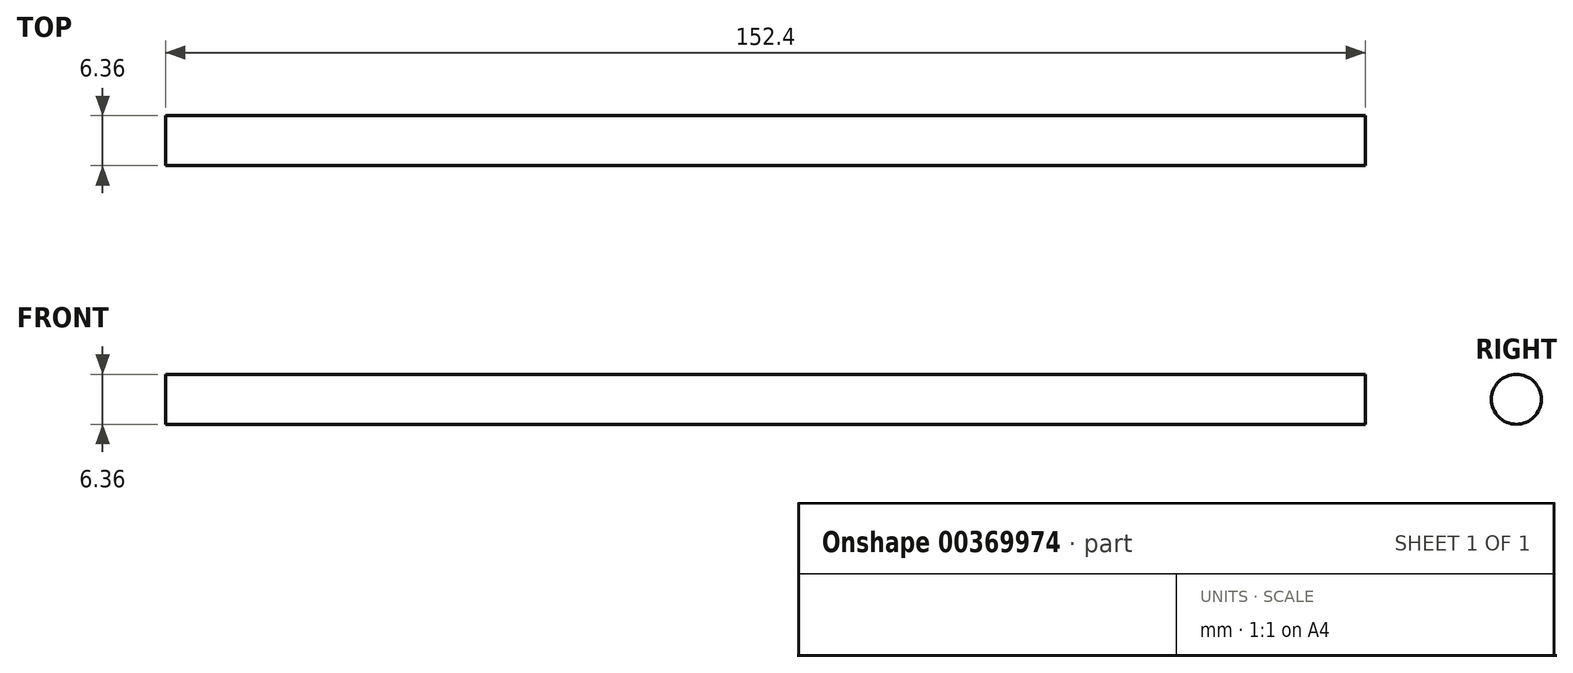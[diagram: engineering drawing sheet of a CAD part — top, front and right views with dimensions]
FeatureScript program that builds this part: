
annotation { "Feature Type Name" : "Feature", "Feature Type Description" : "" }
export const myFeature = defineFeature(function(context is Context, id is Id, definition is map)
    precondition{}
    {
        {
            var Q0;
            Q0=qCreatedBy(makeId("Right.planeOp"),FACE);
            var sketch = newSketch(context, id + "F0", { "sketchPlane" : qUnion([Q0])});
            skCircle(sketch, "E0", {"center": v(0, 0) * mm, "radius": 3.18 * mm});
            skSolve(sketch);
        }
        {
            var Q0;
            Q0=makeQuery(id+"F0.imprint","IMPRINT",FACE,{"disambiguationData":[TD([[makeQuery(id+"F0.imprint","IMPRINT",EDGE,{"derivedFrom":sQuery(id+"F0.wireOp",EDGE,"E0")}),1.0]])]});
            extrude(context, id + "F1", {"entities" : qUnion([Q0]), "endBound" : BoundingType.SYMMETRIC, "depth" : 152.4 * mm});
        }
    });
